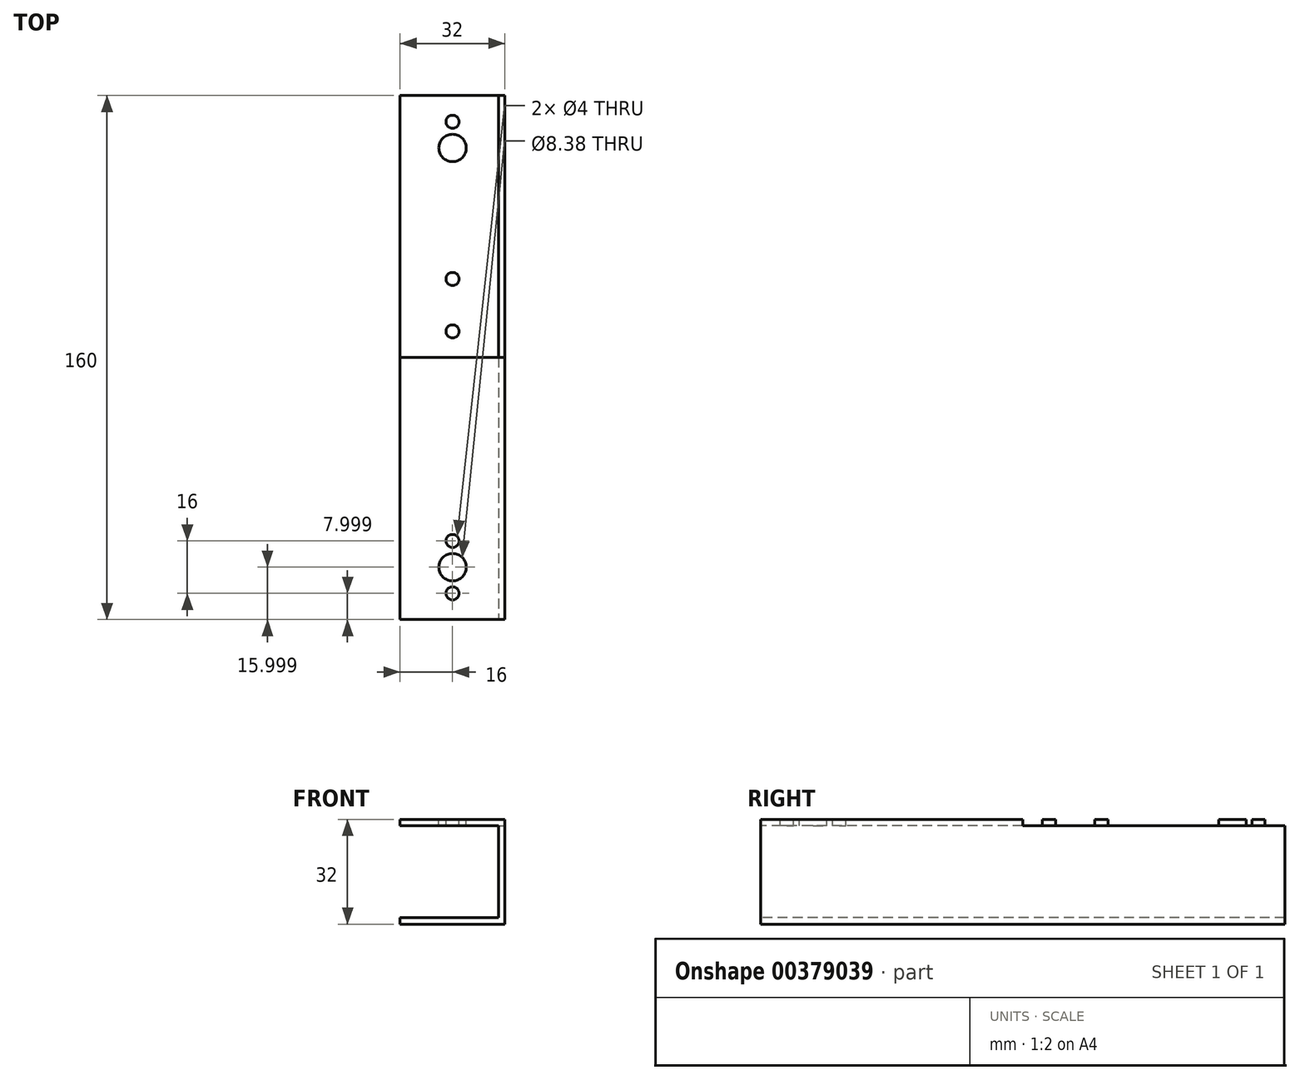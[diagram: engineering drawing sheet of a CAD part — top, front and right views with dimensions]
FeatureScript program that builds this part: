
annotation { "Feature Type Name" : "Feature", "Feature Type Description" : "" }
export const myFeature = defineFeature(function(context is Context, id is Id, definition is map)
    precondition{}
    {
        {
            var Q0;
            Q0=qCreatedBy(makeId("Front.planeOp"),FACE);
            var sketch = newSketch(context, id + "F0", { "sketchPlane" : qUnion([Q0])});
            skLineSegment(sketch, "E0.bottom", {"start": v(0, 0) * mm, "end": v(32, 0) * mm});
            skLineSegment(sketch, "E0.top", {"start": v(0, 32) * mm, "end": v(32, 32) * mm});
            skLineSegment(sketch, "E0.left", {"start": v(0, 0) * mm, "end": v(0, 32) * mm});
            skLineSegment(sketch, "E0.right", {"start": v(32, 0) * mm, "end": v(32, 32) * mm});
            skSolve(sketch);
        }
        {
            var Q0;
            Q0=makeQuery(id+"F0.imprint","IMPRINT",FACE,{"disambiguationData":[TD([[makeQuery(id+"F0.imprint","IMPRINT",EDGE,{"derivedFrom":sQuery(id+"F0.wireOp",EDGE,"E0.bottom")}),1.0]])]});
            extrude(context, id + "F1", {"entities" : qUnion([Q0]), "oppositeDirection" : true, "depth" : 160 * mm});
        }
        {
            var Q0;
            Q0=makeQuery(id+"F1.opExtrude","CAP_FACE",FACE,{"disambiguationData":[OSD([sQuery(id+"F0.wireOp",EDGE,"E0.bottom"),sQuery(id+"F0.wireOp",EDGE,"E0.top"),sQuery(id+"F0.wireOp",EDGE,"E0.left"),sQuery(id+"F0.wireOp",EDGE,"E0.right")])],"isStart":true});
            var Q1;
            Q1=makeQuery(id+"F1.opExtrude","SWEPT_FACE",FACE,{"disambiguationData":[OSD([sQuery(id+"F0.wireOp",EDGE,"E0.left")])]});
            var Q2;
            Q2=makeQuery(id+"F1.opExtrude","CAP_FACE",FACE,{"disambiguationData":[OSD([sQuery(id+"F0.wireOp",EDGE,"E0.bottom"),sQuery(id+"F0.wireOp",EDGE,"E0.top"),sQuery(id+"F0.wireOp",EDGE,"E0.left"),sQuery(id+"F0.wireOp",EDGE,"E0.right")])],"isStart":false});
            shell(context, id + "F2", {"entities" : qUnion([Q0, Q1, Q2]), "thickness" : 2 * mm});
        }
        {
            var Q0;
            Q0=makeQuery(id+"F1.opExtrude","SWEPT_FACE",FACE,{"disambiguationData":[OSD([sQuery(id+"F0.wireOp",EDGE,"E0.top")])]});
            var sketch = newSketch(context, id + "F3", { "sketchPlane" : qUnion([Q0])});
            skLineSegment(sketch, "E1.0", {"start": v(0, 160) * mm, "end": v(0, 0) * mm});
            skLineSegment(sketch, "E2.0", {"start": v(0, 0) * mm, "end": v(32, 0) * mm});
            skLineSegment(sketch, "E3.0", {"start": v(32, 160) * mm, "end": v(32, 0) * mm});
            skLineSegment(sketch, "E4.0", {"start": v(0, 160) * mm, "end": v(32, 160) * mm});
            skLineSegment(sketch, "E5", {"start": v(0, 80) * mm, "end": v(32, 80) * mm});
            skLineSegment(sketch, "E6", {"start": v(16, 0) * mm, "end": v(16, 160) * mm});
            skCircle(sketch, "E7", {"center": v(16, 16) * mm, "radius": 4.2 * mm});
            skCircle(sketch, "E8.cCircle", {"center": v(16, 16) * mm, "radius": 8 * mm, "construction": true});
            skLineSegment(sketch, "E8.0", {"start": v(24, 16) * mm, "end": v(21.66, 10.34) * mm});
            skLineSegment(sketch, "E8.1", {"start": v(21.66, 10.34) * mm, "end": v(16, 8) * mm});
            skLineSegment(sketch, "E8.2", {"start": v(16, 8) * mm, "end": v(10.34, 10.34) * mm});
            skLineSegment(sketch, "E8.3", {"start": v(10.34, 10.34) * mm, "end": v(8, 16) * mm});
            skLineSegment(sketch, "E8.4", {"start": v(8, 16) * mm, "end": v(10.34, 21.66) * mm});
            skLineSegment(sketch, "E8.5", {"start": v(10.34, 21.66) * mm, "end": v(16, 24) * mm});
            skLineSegment(sketch, "E8.6", {"start": v(16, 24) * mm, "end": v(21.66, 21.66) * mm});
            skLineSegment(sketch, "E8.7", {"start": v(21.66, 21.66) * mm, "end": v(24, 16) * mm});
            skCircle(sketch, "E9", {"center": v(16, 24) * mm, "radius": 2 * mm});
            skCircle(sketch, "E10", {"center": v(16, 8) * mm, "radius": 2 * mm});
            skLineSegment(sketch, "E11", {"start": v(16, 24) * mm, "end": v(16, 32) * mm});
            skLineSegment(sketch, "E12", {"start": v(16, 32) * mm, "end": v(16, 40) * mm});
            skCircle(sketch, "E13", {"center": v(16, 40) * mm, "radius": 2 * mm});
            skLineSegment(sketch, "E14", {"start": v(16, 40) * mm, "end": v(16, 48) * mm});
            skLineSegment(sketch, "E15", {"start": v(16, 40) * mm, "end": v(16, 56) * mm});
            skCircle(sketch, "E16", {"center": v(16, 56) * mm, "radius": 2 * mm});
            skLineSegment(sketch, "E17", {"start": v(16, 56) * mm, "end": v(16, 72) * mm});
            skCircle(sketch, "E18", {"center": v(16, 72) * mm, "radius": 2 * mm});
            skCircle(sketch, "E19.MirrorC", {"center": v(16, 88) * mm, "radius": 2 * mm});
            skCircle(sketch, "E20.MirrorC", {"center": v(16, 104) * mm, "radius": 2 * mm});
            skCircle(sketch, "E21.MirrorC", {"center": v(16, 120) * mm, "radius": 2 * mm});
            skCircle(sketch, "E22.MirrorC", {"center": v(16, 136) * mm, "radius": 2 * mm});
            skCircle(sketch, "E23.MirrorC", {"center": v(16, 152) * mm, "radius": 2 * mm});
            skCircle(sketch, "E24.MirrorC", {"center": v(16, 144) * mm, "radius": 4.2 * mm});
            skSolve(sketch);
        }
        {
            var Q0;
            {var subQ1=sQuery(id+"F3.wireOp",EDGE,"E8.6");var subQ3=sQuery(id+"F3.wireOp",EDGE,"E9");var subQ4=makeQuery(id+"F3.imprint","INTERSECT",VERTEX,{"derivedFrom":[subQ1,subQ3]});Q0=makeQuery(id+"F3.imprint","IMPRINT",FACE,{"disambiguationData":[TD([[makeQuery(id+"F3.imprint","IMPRINT",EDGE,{"disambiguationData":[TD([[subQ4,-1.0]])],"derivedFrom":subQ3}),1.0]])]});}
            var Q1;
            {var subQ1=sQuery(id+"F3.wireOp",EDGE,"E8.5");var subQ3=sQuery(id+"F3.wireOp",EDGE,"E9");var subQ4=makeQuery(id+"F3.imprint","INTERSECT",VERTEX,{"derivedFrom":[subQ1,subQ3]});Q1=makeQuery(id+"F3.imprint","IMPRINT",FACE,{"disambiguationData":[TD([[makeQuery(id+"F3.imprint","IMPRINT",EDGE,{"disambiguationData":[TD([[subQ4,1.0]])],"derivedFrom":subQ3}),1.0]])]});}
            var Q2;
            {var subQ1=sQuery(id+"F3.wireOp",EDGE,"E6");var subQ3=sQuery(id+"F3.wireOp",EDGE,"E9");var subQ4=makeQuery(id+"F3.imprint","INTERSECT",VERTEX,{"derivedFrom":[subQ1,subQ3]});Q2=makeQuery(id+"F3.imprint","IMPRINT",FACE,{"disambiguationData":[TD([[makeQuery(id+"F3.imprint","IMPRINT",EDGE,{"disambiguationData":[TD([[subQ4,1.0]])],"derivedFrom":subQ3}),1.0]])]});}
            var Q3;
            {var subQ1=sQuery(id+"F3.wireOp",EDGE,"E6");var subQ3=sQuery(id+"F3.wireOp",EDGE,"E9");var subQ4=makeQuery(id+"F3.imprint","INTERSECT",VERTEX,{"derivedFrom":[subQ1,subQ3]});Q3=makeQuery(id+"F3.imprint","IMPRINT",FACE,{"disambiguationData":[TD([[makeQuery(id+"F3.imprint","IMPRINT",EDGE,{"disambiguationData":[TD([[subQ4,-1.0]])],"derivedFrom":subQ3}),1.0]])]});}
            var Q4;
            {var subQ1=sQuery(id+"F3.wireOp",EDGE,"E6");var subQ3=sQuery(id+"F3.wireOp",EDGE,"E10");var subQ4=makeQuery(id+"F3.imprint","INTERSECT",VERTEX,{"disambiguationData":[OD(1.0)],"derivedFrom":[subQ1,subQ3]});Q4=makeQuery(id+"F3.imprint","IMPRINT",FACE,{"disambiguationData":[TD([[makeQuery(id+"F3.imprint","IMPRINT",EDGE,{"disambiguationData":[TD([[subQ4,-1.0]])],"derivedFrom":subQ3}),1.0]])]});}
            var Q5;
            {var subQ1=sQuery(id+"F3.wireOp",EDGE,"E6");var subQ3=sQuery(id+"F3.wireOp",EDGE,"E10");var subQ4=makeQuery(id+"F3.imprint","INTERSECT",VERTEX,{"disambiguationData":[OD(1.0)],"derivedFrom":[subQ1,subQ3]});Q5=makeQuery(id+"F3.imprint","IMPRINT",FACE,{"disambiguationData":[TD([[makeQuery(id+"F3.imprint","IMPRINT",EDGE,{"disambiguationData":[TD([[subQ4,1.0]])],"derivedFrom":subQ3}),1.0]])]});}
            var Q6;
            {var subQ1=sQuery(id+"F3.wireOp",EDGE,"E6");var subQ3=sQuery(id+"F3.wireOp",EDGE,"E10");var subQ4=makeQuery(id+"F3.imprint","INTERSECT",VERTEX,{"disambiguationData":[OD(0.0)],"derivedFrom":[subQ1,subQ3]});Q6=makeQuery(id+"F3.imprint","IMPRINT",FACE,{"disambiguationData":[TD([[makeQuery(id+"F3.imprint","IMPRINT",EDGE,{"disambiguationData":[TD([[subQ4,-1.0]])],"derivedFrom":subQ3}),1.0]])]});}
            var Q7;
            {var subQ1=sQuery(id+"F3.wireOp",EDGE,"E6");var subQ3=sQuery(id+"F3.wireOp",EDGE,"E10");var subQ4=makeQuery(id+"F3.imprint","INTERSECT",VERTEX,{"disambiguationData":[OD(0.0)],"derivedFrom":[subQ1,subQ3]});Q7=makeQuery(id+"F3.imprint","IMPRINT",FACE,{"disambiguationData":[TD([[makeQuery(id+"F3.imprint","IMPRINT",EDGE,{"disambiguationData":[TD([[subQ4,1.0]])],"derivedFrom":subQ3}),1.0]])]});}
            var Q8;
            {var subQ0=sQuery(id+"F3.wireOp",EDGE,"E15");var subQ1=sQuery(id+"F3.wireOp",EDGE,"E12");var subQ2=makeQuery(id+"F3.imprint","INTERSECT",VERTEX,{"derivedFrom":[subQ1,subQ0]});Q8=makeQuery(id+"F3.imprint","IMPRINT",FACE,{"disambiguationData":[TD([[makeQuery(id+"F3.imprint","IMPRINT",EDGE,{"disambiguationData":[TD([[subQ2,1.0]])],"derivedFrom":subQ1}),-1.0]])]});}
            var Q9;
            {var subQ0=sQuery(id+"F3.wireOp",EDGE,"E15");var subQ1=sQuery(id+"F3.wireOp",EDGE,"E12");var subQ2=makeQuery(id+"F3.imprint","INTERSECT",VERTEX,{"derivedFrom":[subQ1,subQ0]});Q9=makeQuery(id+"F3.imprint","IMPRINT",FACE,{"disambiguationData":[TD([[makeQuery(id+"F3.imprint","IMPRINT",EDGE,{"disambiguationData":[TD([[subQ2,1.0]])],"derivedFrom":subQ1}),1.0]])]});}
            var Q10;
            {var subQ0=sQuery(id+"F3.wireOp",EDGE,"E17");var subQ1=sQuery(id+"F3.wireOp",EDGE,"E15");var subQ2=makeQuery(id+"F3.imprint","INTERSECT",VERTEX,{"derivedFrom":[subQ1,subQ0]});Q10=makeQuery(id+"F3.imprint","IMPRINT",FACE,{"disambiguationData":[TD([[makeQuery(id+"F3.imprint","IMPRINT",EDGE,{"disambiguationData":[TD([[subQ2,1.0]])],"derivedFrom":subQ1}),1.0]])]});}
            var Q11;
            {var subQ0=sQuery(id+"F3.wireOp",EDGE,"E17");var subQ1=sQuery(id+"F3.wireOp",EDGE,"E15");var subQ2=makeQuery(id+"F3.imprint","INTERSECT",VERTEX,{"derivedFrom":[subQ1,subQ0]});Q11=makeQuery(id+"F3.imprint","IMPRINT",FACE,{"disambiguationData":[TD([[makeQuery(id+"F3.imprint","IMPRINT",EDGE,{"disambiguationData":[TD([[subQ2,1.0]])],"derivedFrom":subQ1}),-1.0]])]});}
            var Q12;
            {var subQ0=sQuery(id+"F3.wireOp",EDGE,"E17");var subQ1=sQuery(id+"F3.wireOp",EDGE,"E6");var subQ2=makeQuery(id+"F3.imprint","INTERSECT",VERTEX,{"derivedFrom":[subQ1,subQ0]});Q12=makeQuery(id+"F3.imprint","IMPRINT",FACE,{"disambiguationData":[TD([[makeQuery(id+"F3.imprint","IMPRINT",EDGE,{"disambiguationData":[TD([[subQ2,-1.0]])],"derivedFrom":subQ1}),1.0]])]});}
            var Q13;
            {var subQ0=sQuery(id+"F3.wireOp",EDGE,"E17");var subQ1=sQuery(id+"F3.wireOp",EDGE,"E6");var subQ2=makeQuery(id+"F3.imprint","INTERSECT",VERTEX,{"derivedFrom":[subQ1,subQ0]});Q13=makeQuery(id+"F3.imprint","IMPRINT",FACE,{"disambiguationData":[TD([[makeQuery(id+"F3.imprint","IMPRINT",EDGE,{"disambiguationData":[TD([[subQ2,-1.0]])],"derivedFrom":subQ1}),-1.0]])]});}
            var Q14;
            {var subQ0=sQuery(id+"F3.wireOp",EDGE,"E19.MirrorC");var subQ1=sQuery(id+"F3.wireOp",EDGE,"E6");var subQ2=makeQuery(id+"F3.imprint","INTERSECT",VERTEX,{"disambiguationData":[OD(0.0)],"derivedFrom":[subQ1,subQ0]});Q14=makeQuery(id+"F3.imprint","IMPRINT",FACE,{"disambiguationData":[TD([[makeQuery(id+"F3.imprint","IMPRINT",EDGE,{"disambiguationData":[TD([[subQ2,-1.0]])],"derivedFrom":subQ1}),1.0]])]});}
            var Q15;
            {var subQ0=sQuery(id+"F3.wireOp",EDGE,"E19.MirrorC");var subQ1=sQuery(id+"F3.wireOp",EDGE,"E6");var subQ2=makeQuery(id+"F3.imprint","INTERSECT",VERTEX,{"disambiguationData":[OD(0.0)],"derivedFrom":[subQ1,subQ0]});Q15=makeQuery(id+"F3.imprint","IMPRINT",FACE,{"disambiguationData":[TD([[makeQuery(id+"F3.imprint","IMPRINT",EDGE,{"disambiguationData":[TD([[subQ2,-1.0]])],"derivedFrom":subQ1}),-1.0]])]});}
            var Q16;
            {var subQ0=sQuery(id+"F3.wireOp",EDGE,"E20.MirrorC");var subQ1=sQuery(id+"F3.wireOp",EDGE,"E6");var subQ2=makeQuery(id+"F3.imprint","INTERSECT",VERTEX,{"disambiguationData":[OD(0.0)],"derivedFrom":[subQ1,subQ0]});Q16=makeQuery(id+"F3.imprint","IMPRINT",FACE,{"disambiguationData":[TD([[makeQuery(id+"F3.imprint","IMPRINT",EDGE,{"disambiguationData":[TD([[subQ2,-1.0]])],"derivedFrom":subQ1}),-1.0]])]});}
            var Q17;
            {var subQ0=sQuery(id+"F3.wireOp",EDGE,"E20.MirrorC");var subQ1=sQuery(id+"F3.wireOp",EDGE,"E6");var subQ2=makeQuery(id+"F3.imprint","INTERSECT",VERTEX,{"disambiguationData":[OD(0.0)],"derivedFrom":[subQ1,subQ0]});Q17=makeQuery(id+"F3.imprint","IMPRINT",FACE,{"disambiguationData":[TD([[makeQuery(id+"F3.imprint","IMPRINT",EDGE,{"disambiguationData":[TD([[subQ2,-1.0]])],"derivedFrom":subQ1}),1.0]])]});}
            var Q18;
            {var subQ0=sQuery(id+"F3.wireOp",EDGE,"E21.MirrorC");var subQ1=sQuery(id+"F3.wireOp",EDGE,"E6");var subQ2=makeQuery(id+"F3.imprint","INTERSECT",VERTEX,{"disambiguationData":[OD(0.0)],"derivedFrom":[subQ1,subQ0]});Q18=makeQuery(id+"F3.imprint","IMPRINT",FACE,{"disambiguationData":[TD([[makeQuery(id+"F3.imprint","IMPRINT",EDGE,{"disambiguationData":[TD([[subQ2,-1.0]])],"derivedFrom":subQ1}),1.0]])]});}
            var Q19;
            {var subQ0=sQuery(id+"F3.wireOp",EDGE,"E21.MirrorC");var subQ1=sQuery(id+"F3.wireOp",EDGE,"E6");var subQ2=makeQuery(id+"F3.imprint","INTERSECT",VERTEX,{"disambiguationData":[OD(0.0)],"derivedFrom":[subQ1,subQ0]});Q19=makeQuery(id+"F3.imprint","IMPRINT",FACE,{"disambiguationData":[TD([[makeQuery(id+"F3.imprint","IMPRINT",EDGE,{"disambiguationData":[TD([[subQ2,-1.0]])],"derivedFrom":subQ1}),-1.0]])]});}
            var Q20;
            {var subQ0=sQuery(id+"F3.wireOp",EDGE,"E22.MirrorC");var subQ1=sQuery(id+"F3.wireOp",EDGE,"E6");var subQ2=makeQuery(id+"F3.imprint","INTERSECT",VERTEX,{"disambiguationData":[OD(0.0)],"derivedFrom":[subQ1,subQ0]});Q20=makeQuery(id+"F3.imprint","IMPRINT",FACE,{"disambiguationData":[TD([[makeQuery(id+"F3.imprint","IMPRINT",EDGE,{"disambiguationData":[TD([[subQ2,-1.0]])],"derivedFrom":subQ1}),1.0]])]});}
            var Q21;
            {var subQ0=sQuery(id+"F3.wireOp",EDGE,"E22.MirrorC");var subQ1=sQuery(id+"F3.wireOp",EDGE,"E6");var subQ2=makeQuery(id+"F3.imprint","INTERSECT",VERTEX,{"disambiguationData":[OD(0.0)],"derivedFrom":[subQ1,subQ0]});Q21=makeQuery(id+"F3.imprint","IMPRINT",FACE,{"disambiguationData":[TD([[makeQuery(id+"F3.imprint","IMPRINT",EDGE,{"disambiguationData":[TD([[subQ2,-1.0]])],"derivedFrom":subQ1}),-1.0]])]});}
            var Q22;
            {var subQ0=sQuery(id+"F3.wireOp",EDGE,"E23.MirrorC");var subQ1=sQuery(id+"F3.wireOp",EDGE,"E6");var subQ2=makeQuery(id+"F3.imprint","INTERSECT",VERTEX,{"disambiguationData":[OD(0.0)],"derivedFrom":[subQ1,subQ0]});Q22=makeQuery(id+"F3.imprint","IMPRINT",FACE,{"disambiguationData":[TD([[makeQuery(id+"F3.imprint","IMPRINT",EDGE,{"disambiguationData":[TD([[subQ2,-1.0]])],"derivedFrom":subQ1}),1.0]])]});}
            var Q23;
            {var subQ0=sQuery(id+"F3.wireOp",EDGE,"E23.MirrorC");var subQ1=sQuery(id+"F3.wireOp",EDGE,"E6");var subQ2=makeQuery(id+"F3.imprint","INTERSECT",VERTEX,{"disambiguationData":[OD(0.0)],"derivedFrom":[subQ1,subQ0]});Q23=makeQuery(id+"F3.imprint","IMPRINT",FACE,{"disambiguationData":[TD([[makeQuery(id+"F3.imprint","IMPRINT",EDGE,{"disambiguationData":[TD([[subQ2,-1.0]])],"derivedFrom":subQ1}),-1.0]])]});}
            var Q24;
            {var subQ0=sQuery(id+"F3.wireOp",EDGE,"E7");var subQ1=sQuery(id+"F3.wireOp",EDGE,"E6");var subQ2=makeQuery(id+"F3.imprint","INTERSECT",VERTEX,{"disambiguationData":[OD(0.0)],"derivedFrom":[subQ1,subQ0]});Q24=makeQuery(id+"F3.imprint","IMPRINT",FACE,{"disambiguationData":[TD([[makeQuery(id+"F3.imprint","IMPRINT",EDGE,{"disambiguationData":[TD([[subQ2,-1.0]])],"derivedFrom":subQ1}),1.0]])]});}
            var Q25;
            {var subQ0=sQuery(id+"F3.wireOp",EDGE,"E7");var subQ1=sQuery(id+"F3.wireOp",EDGE,"E6");var subQ2=makeQuery(id+"F3.imprint","INTERSECT",VERTEX,{"disambiguationData":[OD(0.0)],"derivedFrom":[subQ1,subQ0]});Q25=makeQuery(id+"F3.imprint","IMPRINT",FACE,{"disambiguationData":[TD([[makeQuery(id+"F3.imprint","IMPRINT",EDGE,{"disambiguationData":[TD([[subQ2,-1.0]])],"derivedFrom":subQ1}),-1.0]])]});}
            var Q26;
            {var subQ0=sQuery(id+"F3.wireOp",EDGE,"E24.MirrorC");var subQ1=sQuery(id+"F3.wireOp",EDGE,"E6");var subQ2=makeQuery(id+"F3.imprint","INTERSECT",VERTEX,{"disambiguationData":[OD(0.0)],"derivedFrom":[subQ1,subQ0]});Q26=makeQuery(id+"F3.imprint","IMPRINT",FACE,{"disambiguationData":[TD([[makeQuery(id+"F3.imprint","IMPRINT",EDGE,{"disambiguationData":[TD([[subQ2,-1.0]])],"derivedFrom":subQ1}),1.0]])]});}
            var Q27;
            {var subQ0=sQuery(id+"F3.wireOp",EDGE,"E24.MirrorC");var subQ1=sQuery(id+"F3.wireOp",EDGE,"E6");var subQ2=makeQuery(id+"F3.imprint","INTERSECT",VERTEX,{"disambiguationData":[OD(0.0)],"derivedFrom":[subQ1,subQ0]});Q27=makeQuery(id+"F3.imprint","IMPRINT",FACE,{"disambiguationData":[TD([[makeQuery(id+"F3.imprint","IMPRINT",EDGE,{"disambiguationData":[TD([[subQ2,-1.0]])],"derivedFrom":subQ1}),-1.0]])]});}
            var Q28;
            Q28=makeQuery(id+"F2.opShell","OFFSET_FACE",FACE,{"disambiguationData":[OSD([sQuery(id+"F0.wireOp",EDGE,"E0.top")])]});
            extrude(context, id + "F4", {"entities" : qUnion([Q0, Q1, Q2, Q3, Q4, Q5, Q6, Q7, Q8, Q9, Q10, Q11, Q12, Q13, Q14, Q15, Q16, Q17, Q18, Q19, Q20, Q21, Q22, Q23, Q24, Q25, Q26, Q27]), "operationType" : NewBodyOperationType.REMOVE, "endBound" : BoundingType.UP_TO_SURFACE, "oppositeDirection" : true, "endBoundEntityFace" : qUnion([Q28]), "depth" : 25.4 * mm});
        }
    });
